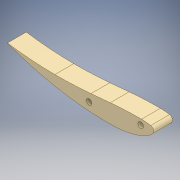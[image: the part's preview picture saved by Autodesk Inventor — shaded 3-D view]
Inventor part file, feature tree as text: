
AUTODESK INVENTOR PART (.ipt)
format: ipt  version: 2018 (Build 220112000, 112)  size: 122,368 bytes
history: native  units: mm
features: extrude x1, sketch x1, projected_geometry x1
ambient origin geometry x8: Origin, YZ Plane, XZ Plane, XY Plane, X Axis, Y Axis, Z Axis, Center Point
bodies: Body1 (feature_tree)
feature tree (3):
  extrude  "押し出し2"  Depth=40.2mm TaperAngle=0.0deg
  sketch  "スケッチ1"
  projected_geometry  "投影ループ1"
